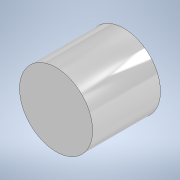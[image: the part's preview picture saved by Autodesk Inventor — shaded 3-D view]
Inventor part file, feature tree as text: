
AUTODESK INVENTOR PART (.ipt)
format: ipt  version: 2021 (Build 250183000, 183)  size: 93,184 bytes
history: native  units: mm
features: extrude x1, sketch x1
ambient origin geometry x8: Origin, YZ Plane, XZ Plane, XY Plane, X Axis, Y Axis, Z Axis, Center Point
bodies: Solid1 (feature_tree)
feature tree (2):
  extrude  "Extrusion1"  Depth=6.5mm TaperAngle=0.0deg
  sketch  "Sketch1"  dims[d0=7.0mm d1=6.5mm d2=0.0mm]
